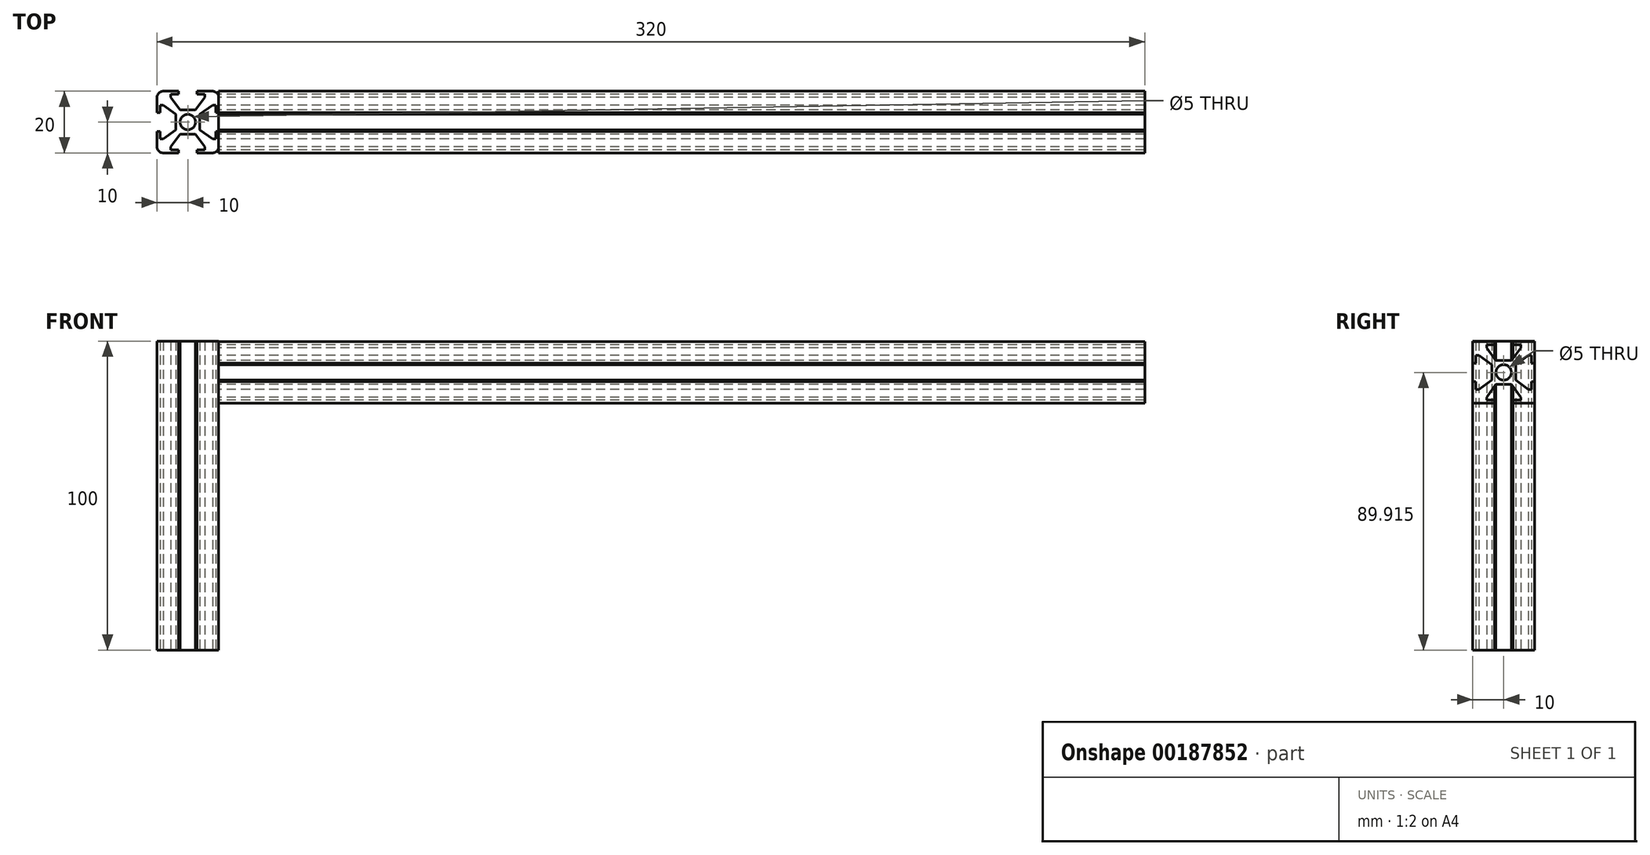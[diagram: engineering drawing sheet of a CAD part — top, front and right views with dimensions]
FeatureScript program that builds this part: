
annotation { "Feature Type Name" : "Feature", "Feature Type Description" : "" }
export const myFeature = defineFeature(function(context is Context, id is Id, definition is map)
    precondition{}
    {
        {
            var Q0;
            Q0=qCreatedBy(makeId("Top.planeOp"),FACE);
            var sketch = newSketch(context, id + "F0", { "sketchPlane" : qUnion([Q0])});
            skLineSegment(sketch, "E0.bottom", {"start": v(-10, 10) * mm, "end": v(-3, 10) * mm});
            skLineSegment(sketch, "E0.top", {"start": v(-10, -10) * mm, "end": v(-3, -10) * mm});
            skLineSegment(sketch, "E0.left", {"start": v(-10, 10) * mm, "end": v(-10, 3) * mm});
            skLineSegment(sketch, "E0.right", {"start": v(10, 10) * mm, "end": v(10, 3) * mm});
            skPoint(sketch, "E0.middle", {"position": v(0, 0) * mm});
            skLineSegment(sketch, "E1.left", {"start": v(-3, -9) * mm, "end": v(-3, -10) * mm});
            skLineSegment(sketch, "E1.right", {"start": v(3, -9) * mm, "end": v(3, -10) * mm});
            skPoint(sketch, "E1.middle", {"position": v(0, -10) * mm});
            skLineSegment(sketch, "E2.trimOffspring", {"start": v(3, -10) * mm, "end": v(10, -10) * mm});
            skLineSegment(sketch, "E3", {"start": v(-3, -9) * mm, "end": v(-5.5, -9) * mm});
            skLineSegment(sketch, "E4", {"start": v(-5.5, -9) * mm, "end": v(-5.5, -8) * mm});
            skLineSegment(sketch, "E5", {"start": v(5.5, -9) * mm, "end": v(3, -9) * mm});
            skPoint(sketch, "E6.bottom.end.orphan", {"position": v(4.03, 4.03) * mm});
            skPoint(sketch, "E6.bottom.start.orphan", {"position": v(-4.03, 4.03) * mm});
            skLineSegment(sketch, "E7", {"start": v(-5.5, -8) * mm, "end": v(-2.5, -3.9) * mm});
            skLineSegment(sketch, "E8", {"start": v(-2.5, -3.9) * mm, "end": v(2.5, -3.9) * mm});
            skLineSegment(sketch, "E9", {"start": v(2.5, -3.9) * mm, "end": v(5.5, -8) * mm});
            skLineSegment(sketch, "E10", {"start": v(5.5, -8) * mm, "end": v(5.5, -9) * mm});
            skLineSegment(sketch, "E11.1.0", {"start": v(3.9, 2.5) * mm, "end": v(8, 5.5) * mm});
            skLineSegment(sketch, "E11.1.1", {"start": v(3.9, -2.5) * mm, "end": v(3.9, 2.5) * mm});
            skLineSegment(sketch, "E11.1.2", {"start": v(8, -5.5) * mm, "end": v(3.9, -2.5) * mm});
            skLineSegment(sketch, "E11.1.3", {"start": v(9, 5.5) * mm, "end": v(9, 3) * mm});
            skLineSegment(sketch, "E11.1.4", {"start": v(9, -5.5) * mm, "end": v(8, -5.5) * mm});
            skLineSegment(sketch, "E11.1.5", {"start": v(9, -3) * mm, "end": v(9, -5.5) * mm});
            skLineSegment(sketch, "E11.1.6", {"start": v(8, 5.5) * mm, "end": v(9, 5.5) * mm});
            skLineSegment(sketch, "E11.1.7", {"start": v(9, 3) * mm, "end": v(10, 3) * mm});
            skLineSegment(sketch, "E11.1.8", {"start": v(9, -3) * mm, "end": v(10, -3) * mm});
            skLineSegment(sketch, "E11.2.0", {"start": v(-2.5, 3.9) * mm, "end": v(-5.5, 8) * mm});
            skLineSegment(sketch, "E11.2.1", {"start": v(2.5, 3.9) * mm, "end": v(-2.5, 3.9) * mm});
            skLineSegment(sketch, "E11.2.2", {"start": v(5.5, 8) * mm, "end": v(2.5, 3.9) * mm});
            skLineSegment(sketch, "E11.2.3", {"start": v(-5.5, 9) * mm, "end": v(-3, 9) * mm});
            skLineSegment(sketch, "E11.2.4", {"start": v(5.5, 9) * mm, "end": v(5.5, 8) * mm});
            skLineSegment(sketch, "E11.2.5", {"start": v(3, 9) * mm, "end": v(5.5, 9) * mm});
            skLineSegment(sketch, "E11.2.6", {"start": v(-5.5, 8) * mm, "end": v(-5.5, 9) * mm});
            skLineSegment(sketch, "E11.2.7", {"start": v(-3, 9) * mm, "end": v(-3, 10) * mm});
            skLineSegment(sketch, "E11.2.8", {"start": v(3, 9) * mm, "end": v(3, 10) * mm});
            skLineSegment(sketch, "E11.3.0", {"start": v(-3.9, -2.5) * mm, "end": v(-8, -5.5) * mm});
            skLineSegment(sketch, "E11.3.1", {"start": v(-3.9, 2.5) * mm, "end": v(-3.9, -2.5) * mm});
            skLineSegment(sketch, "E11.3.2", {"start": v(-8, 5.5) * mm, "end": v(-3.9, 2.5) * mm});
            skLineSegment(sketch, "E11.3.3", {"start": v(-9, -5.5) * mm, "end": v(-9, -3) * mm});
            skLineSegment(sketch, "E11.3.4", {"start": v(-9, 5.5) * mm, "end": v(-8, 5.5) * mm});
            skLineSegment(sketch, "E11.3.5", {"start": v(-9, 3) * mm, "end": v(-9, 5.5) * mm});
            skLineSegment(sketch, "E11.3.6", {"start": v(-8, -5.5) * mm, "end": v(-9, -5.5) * mm});
            skLineSegment(sketch, "E11.3.7", {"start": v(-9, -3) * mm, "end": v(-10, -3) * mm});
            skLineSegment(sketch, "E11.3.8", {"start": v(-9, 3) * mm, "end": v(-10, 3) * mm});
            skLineSegment(sketch, "E12.trimOffspring", {"start": v(-10, -3) * mm, "end": v(-10, -10) * mm});
            skLineSegment(sketch, "E13.trimOffspring", {"start": v(3, 10) * mm, "end": v(10, 10) * mm});
            skLineSegment(sketch, "E14.trimOffspring", {"start": v(10, -3) * mm, "end": v(10, -10) * mm});
            skCircle(sketch, "E15", {"center": v(0, 0) * mm, "radius": 2.5 * mm});
            skSolve(sketch);
        }
        {
            var Q0;
            Q0 = qSketchRegion(id + "F0", true);
            extrude(context, id + "F1", {"entities" : qUnion([Q0]), "endBound" : BoundingType.SYMMETRIC, "depth" : 100 * mm});
        }
        {
            var Q0;
            Q0=makeQuery(id+"F1.opExtrude","SWEPT_EDGE",EDGE,{"disambiguationData":[OSD([sQuery(id+"F0.wireOp",EDGE,"E0.top"),sQuery(id+"F0.wireOp",EDGE,"E12.trimOffspring")])]});
            var Q1;
            Q1=makeQuery(id+"F1.opExtrude","SWEPT_EDGE",EDGE,{"disambiguationData":[OSD([sQuery(id+"F0.wireOp",EDGE,"E2.trimOffspring"),sQuery(id+"F0.wireOp",EDGE,"E14.trimOffspring")])]});
            var Q2;
            Q2=makeQuery(id+"F1.opExtrude","SWEPT_EDGE",EDGE,{"disambiguationData":[OSD([sQuery(id+"F0.wireOp",EDGE,"E0.right"),sQuery(id+"F0.wireOp",EDGE,"E13.trimOffspring")])]});
            var Q3;
            Q3=makeQuery(id+"F1.opExtrude","SWEPT_EDGE",EDGE,{"disambiguationData":[OSD([sQuery(id+"F0.wireOp",EDGE,"E0.bottom"),sQuery(id+"F0.wireOp",EDGE,"E0.left")])]});
            fillet(context, id + "F2", {"entities" : qUnion([Q0, Q1, Q2, Q3]), "radius" : 2 * mm, "tangentPropagation" : true, "allowEdgeOverflow" : false});
        }
        {
            var Q0;
            Q0=makeQuery(id+"F1.opExtrude","SWEPT_FACE",FACE,{"disambiguationData":[OSD([sQuery(id+"F0.wireOp",EDGE,"E0.right")])]});
            var sketch = newSketch(context, id + "F3", { "sketchPlane" : qUnion([Q0])});
            skLineSegment(sketch, "E16.bottom", {"start": v(-10, 49.91) * mm, "end": v(-3, 49.91) * mm});
            skLineSegment(sketch, "E16.top", {"start": v(-10, 29.91) * mm, "end": v(-3, 29.91) * mm});
            skLineSegment(sketch, "E16.left", {"start": v(-10, 49.91) * mm, "end": v(-10, 42.91) * mm});
            skLineSegment(sketch, "E16.right", {"start": v(10, 49.91) * mm, "end": v(10, 42.91) * mm});
            skPoint(sketch, "E16.middle", {"position": v(0, 39.91) * mm});
            skLineSegment(sketch, "E17.left", {"start": v(-3, 30.91) * mm, "end": v(-3, 29.91) * mm});
            skLineSegment(sketch, "E17.right", {"start": v(3, 30.91) * mm, "end": v(3, 29.91) * mm});
            skPoint(sketch, "E17.middle", {"position": v(0, 29.91) * mm});
            skLineSegment(sketch, "E18.trimOffspring", {"start": v(3, 29.91) * mm, "end": v(10, 29.91) * mm});
            skLineSegment(sketch, "E19", {"start": v(-3, 30.91) * mm, "end": v(-5.5, 30.91) * mm});
            skLineSegment(sketch, "E20", {"start": v(-5.5, 30.91) * mm, "end": v(-5.5, 31.91) * mm});
            skLineSegment(sketch, "E21", {"start": v(5.5, 30.91) * mm, "end": v(3, 30.91) * mm});
            skPoint(sketch, "E22.bottom.end.orphan", {"position": v(4.29, 47.71) * mm});
            skPoint(sketch, "E22.bottom.start.orphan", {"position": v(-3.78, 47.71) * mm});
            skLineSegment(sketch, "E23", {"start": v(-5.5, 31.91) * mm, "end": v(-2.5, 36.01) * mm});
            skLineSegment(sketch, "E24", {"start": v(-2.5, 36.01) * mm, "end": v(2.5, 36.01) * mm});
            skLineSegment(sketch, "E25", {"start": v(2.5, 36.01) * mm, "end": v(5.5, 31.91) * mm});
            skLineSegment(sketch, "E26", {"start": v(5.5, 31.91) * mm, "end": v(5.5, 30.91) * mm});
            skLineSegment(sketch, "E27.1.0", {"start": v(3.9, 42.41) * mm, "end": v(8, 45.41) * mm});
            skLineSegment(sketch, "E27.1.1", {"start": v(3.9, 37.41) * mm, "end": v(3.9, 42.41) * mm});
            skLineSegment(sketch, "E27.1.2", {"start": v(8, 34.41) * mm, "end": v(3.9, 37.41) * mm});
            skLineSegment(sketch, "E27.1.3", {"start": v(9, 45.41) * mm, "end": v(9, 42.91) * mm});
            skLineSegment(sketch, "E27.1.4", {"start": v(9, 34.41) * mm, "end": v(8, 34.41) * mm});
            skLineSegment(sketch, "E27.1.5", {"start": v(9, 36.91) * mm, "end": v(9, 34.41) * mm});
            skLineSegment(sketch, "E27.1.6", {"start": v(8, 45.41) * mm, "end": v(9, 45.41) * mm});
            skLineSegment(sketch, "E27.1.7", {"start": v(9, 42.91) * mm, "end": v(10, 42.91) * mm});
            skLineSegment(sketch, "E27.1.8", {"start": v(9, 36.91) * mm, "end": v(10, 36.91) * mm});
            skLineSegment(sketch, "E27.2.0", {"start": v(-2.5, 43.81) * mm, "end": v(-5.5, 47.91) * mm});
            skLineSegment(sketch, "E27.2.1", {"start": v(2.5, 43.81) * mm, "end": v(-2.5, 43.81) * mm});
            skLineSegment(sketch, "E27.2.2", {"start": v(5.5, 47.91) * mm, "end": v(2.5, 43.81) * mm});
            skLineSegment(sketch, "E27.2.3", {"start": v(-5.5, 48.91) * mm, "end": v(-3, 48.91) * mm});
            skLineSegment(sketch, "E27.2.4", {"start": v(5.5, 48.91) * mm, "end": v(5.5, 47.91) * mm});
            skLineSegment(sketch, "E27.2.5", {"start": v(3, 48.91) * mm, "end": v(5.5, 48.91) * mm});
            skLineSegment(sketch, "E27.2.6", {"start": v(-5.5, 47.91) * mm, "end": v(-5.5, 48.91) * mm});
            skLineSegment(sketch, "E27.2.7", {"start": v(-3, 48.91) * mm, "end": v(-3, 49.91) * mm});
            skLineSegment(sketch, "E27.2.8", {"start": v(3, 48.91) * mm, "end": v(3, 49.91) * mm});
            skLineSegment(sketch, "E27.3.0", {"start": v(-3.9, 37.41) * mm, "end": v(-8, 34.41) * mm});
            skLineSegment(sketch, "E27.3.1", {"start": v(-3.9, 42.41) * mm, "end": v(-3.9, 37.41) * mm});
            skLineSegment(sketch, "E27.3.2", {"start": v(-8, 45.41) * mm, "end": v(-3.9, 42.41) * mm});
            skLineSegment(sketch, "E27.3.3", {"start": v(-9, 34.41) * mm, "end": v(-9, 36.91) * mm});
            skLineSegment(sketch, "E27.3.4", {"start": v(-9, 45.41) * mm, "end": v(-8, 45.41) * mm});
            skLineSegment(sketch, "E27.3.5", {"start": v(-9, 42.91) * mm, "end": v(-9, 45.41) * mm});
            skLineSegment(sketch, "E27.3.6", {"start": v(-8, 34.41) * mm, "end": v(-9, 34.41) * mm});
            skLineSegment(sketch, "E27.3.7", {"start": v(-9, 36.91) * mm, "end": v(-10, 36.91) * mm});
            skLineSegment(sketch, "E27.3.8", {"start": v(-9, 42.91) * mm, "end": v(-10, 42.91) * mm});
            skLineSegment(sketch, "E28.trimOffspring", {"start": v(-10, 36.91) * mm, "end": v(-10, 29.91) * mm});
            skLineSegment(sketch, "E29.trimOffspring", {"start": v(3, 49.91) * mm, "end": v(10, 49.91) * mm});
            skLineSegment(sketch, "E30.trimOffspring", {"start": v(10, 36.91) * mm, "end": v(10, 29.91) * mm});
            skCircle(sketch, "E31", {"center": v(0, 39.91) * mm, "radius": 2.5 * mm});
            skSolve(sketch);
        }
        {
            var Q0;
            Q0 = qSketchRegion(id + "F3", true);
            extrude(context, id + "F4", {"entities" : qUnion([Q0]), "depth" : 300 * mm});
        }
    });
